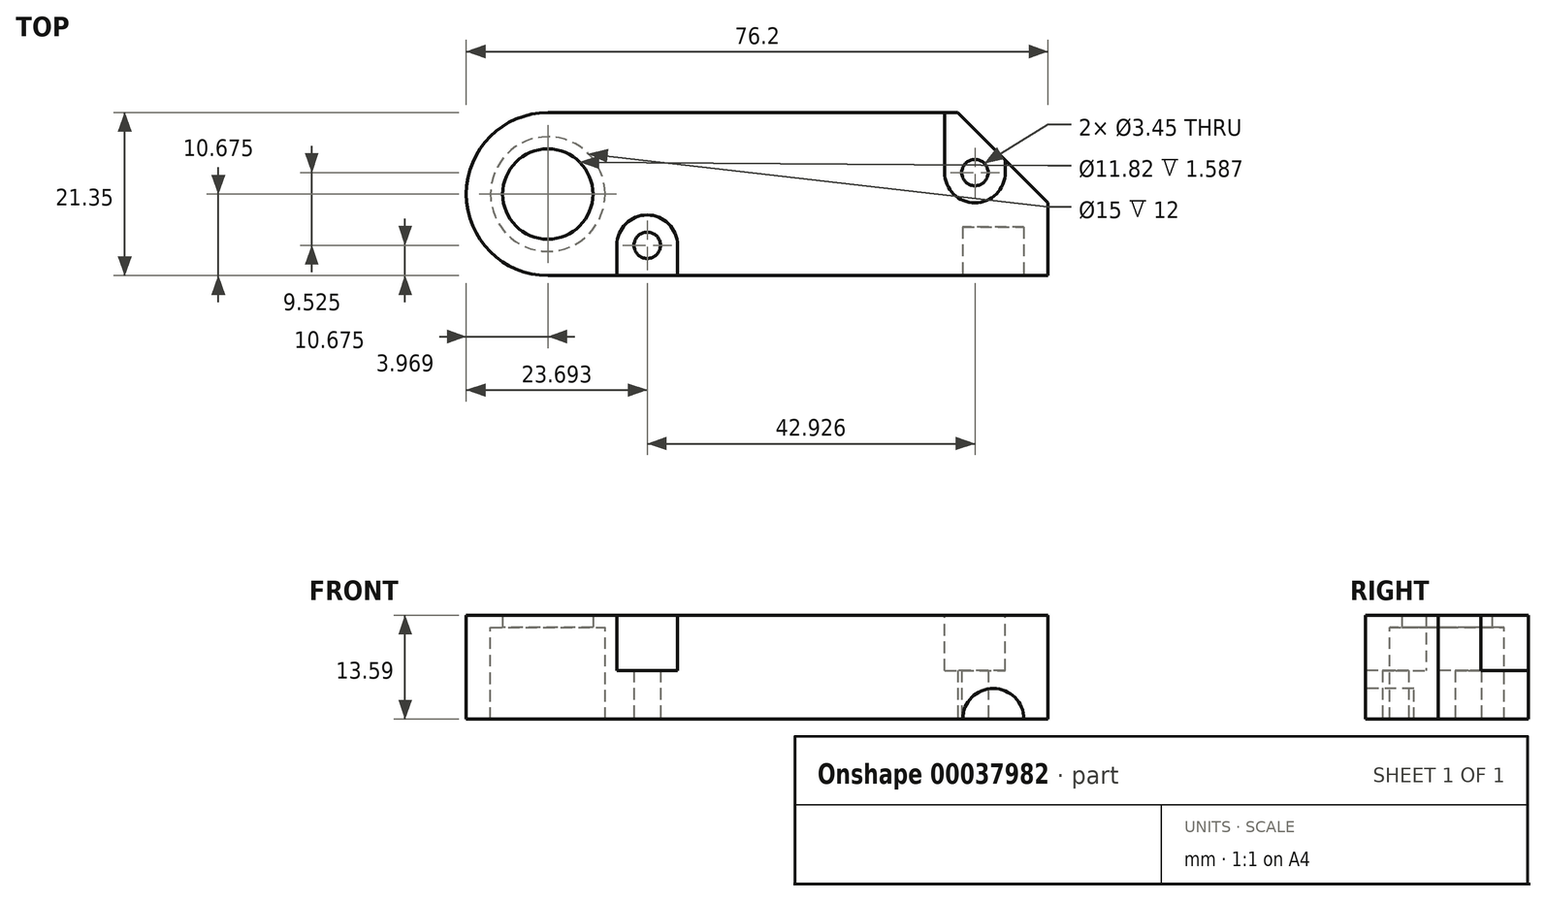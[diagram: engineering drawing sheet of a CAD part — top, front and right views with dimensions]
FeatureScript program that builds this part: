
annotation { "Feature Type Name" : "Feature", "Feature Type Description" : "" }
export const myFeature = defineFeature(function(context is Context, id is Id, definition is map)
    precondition{}
    {
        {
            var Q0;
            Q0=qCreatedBy(makeId("Top.planeOp"),FACE);
            var sketch = newSketch(context, id + "F0", { "sketchPlane" : qUnion([Q0])});
            skLineSegment(sketch, "E0.bottom", {"start": v(0, 0) * mm, "end": v(64.38, 0) * mm});
            skLineSegment(sketch, "E0.top", {"start": v(0, -21.35) * mm, "end": v(76.2, -21.35) * mm});
            skCircle(sketch, "E1", {"center": v(10.67, -10.67) * mm, "radius": 10.67 * mm, "construction": true});
            skLineSegment(sketch, "E2", {"start": v(0, 0) * mm, "end": v(0, -21.35) * mm});
            skLineSegment(sketch, "E3", {"start": v(76.2, -21.35) * mm, "end": v(76.2, -11.82) * mm});
            skLineSegment(sketch, "E4", {"start": v(76.2, -11.82) * mm, "end": v(64.38, 0) * mm});
            skCircle(sketch, "E5", {"center": v(10.67, -10.67) * mm, "radius": 5.91 * mm});
            skLineSegment(sketch, "E6", {"start": v(76.2, -11.82) * mm, "end": v(61.85, -11.82) * mm, "construction": true});
            skLineSegment(sketch, "E7", {"start": v(61.85, -11.82) * mm, "end": v(61.85, -21.35) * mm, "construction": true});
            skCircle(sketch, "E8", {"center": v(23.7, -17.38) * mm, "radius": 3.97 * mm, "construction": true});
            skCircle(sketch, "E9", {"center": v(66.62, -7.86) * mm, "radius": 3.97 * mm, "construction": true});
            skCircle(sketch, "E10", {"center": v(23.7, -17.38) * mm, "radius": 1.73 * mm});
            skCircle(sketch, "E11", {"center": v(66.62, -7.86) * mm, "radius": 1.73 * mm});
            skSolve(sketch);
        }
        {
            var Q0;
            Q0=qSketchRegion(id+"F0",true);
            extrude(context, id + "F1", {"entities" : qUnion([Q0]), "depth" : 1.59 * mm});
        }
        {
            var Q0;
            Q0=makeQuery(id+"F1.opExtrude","CAP_FACE",FACE,{"disambiguationData":[OSD([sQuery(id+"F0.wireOp",EDGE,"E0.bottom"),sQuery(id+"F0.wireOp",EDGE,"E0.top"),sQuery(id+"F0.wireOp",EDGE,"E2"),sQuery(id+"F0.wireOp",EDGE,"E3"),sQuery(id+"F0.wireOp",EDGE,"E4"),sQuery(id+"F0.wireOp",EDGE,"E5"),sQuery(id+"F0.wireOp",EDGE,"E10"),sQuery(id+"F0.wireOp",EDGE,"E11")])],"isStart":true});
            var sketch = newSketch(context, id + "F2", { "sketchPlane" : qUnion([Q0])});
            skCircle(sketch, "E12", {"center": v(10.67, 10.67) * mm, "radius": 7.5 * mm});
            skSolve(sketch);
        }
        {
            var Q0;
            Q0=makeQuery(id+"F2.imprint","IMPRINT",FACE,{"disambiguationData":[TD([[makeQuery(id+"F2.imprint","IMPRINT",EDGE,{"derivedFrom":sQuery(id+"F2.wireOp",EDGE,"E12")}),-1.0]])]});
            extrude(context, id + "F3", {"entities" : qUnion([Q0]), "operationType" : NewBodyOperationType.ADD, "depth" : 12 * mm});
        }
        {
            var Q0;
            {var subQ0=sQuery(id+"F0.wireOp",EDGE,"E0.top");Q0=makeQuery(id+"F3.boolean.opBoolean","MERGE",FACE,{"derivedFrom":[makeQuery(id+"F1.opExtrude","SWEPT_FACE",FACE,{"disambiguationData":[OSD([subQ0])]}),makeQuery(id+"F3.opExtrude","SWEPT_FACE",FACE,{"disambiguationData":[OSD([subQ0])]})]});}
            var sketch = newSketch(context, id + "F4", { "sketchPlane" : qUnion([Q0])});
            skLineSegment(sketch, "E13", {"start": v(76.2, -12) * mm, "end": v(73.03, -12) * mm});
            skLineSegment(sketch, "E14", {"start": v(73.03, -12) * mm, "end": v(65.03, -12) * mm});
            skArc(sketch, "E15", {"start": v(73.03, -12) * mm, "mid": v(69.03, -8) * mm, "end": v(65.03, -12) * mm});
            skSolve(sketch);
        }
        {
            var Q0;
            Q0=qSketchRegion(id+"F4",true);
            extrude(context, id + "F5", {"entities" : qUnion([Q0]), "operationType" : NewBodyOperationType.REMOVE, "oppositeDirection" : true, "depth" : 6.35 * mm});
        }
        {
            var Q0;
            {var subQ0=sQuery(id+"F0.wireOp",EDGE,"E2");var subQ1=sQuery(id+"F0.wireOp",EDGE,"E0.top");Q0=makeQuery(id+"F3.boolean.opBoolean","MERGE",EDGE,{"derivedFrom":[makeQuery(id+"F1.opExtrude","SWEPT_EDGE",EDGE,{"disambiguationData":[OSD([subQ1,subQ0])]}),makeQuery(id+"F3.opExtrude","SWEPT_EDGE",EDGE,{"disambiguationData":[OSD([subQ1,subQ0])]})]});}
            var Q1;
            {var subQ0=sQuery(id+"F0.wireOp",EDGE,"E2");var subQ1=sQuery(id+"F0.wireOp",EDGE,"E0.bottom");Q1=makeQuery(id+"F3.boolean.opBoolean","MERGE",EDGE,{"derivedFrom":[makeQuery(id+"F1.opExtrude","SWEPT_EDGE",EDGE,{"disambiguationData":[OSD([subQ1,subQ0])]}),makeQuery(id+"F3.opExtrude","SWEPT_EDGE",EDGE,{"disambiguationData":[OSD([subQ1,subQ0])]})]});}
            fillet(context, id + "F6", {"entities" : qUnion([Q0, Q1]), "radius" : 10.67 * mm, "tangentPropagation" : true, "allowEdgeOverflow" : false});
        }
        {
            var Q0;
            Q0=makeQuery(id+"F1.opExtrude","CAP_FACE",FACE,{"disambiguationData":[OSD([sQuery(id+"F0.wireOp",EDGE,"E0.bottom"),sQuery(id+"F0.wireOp",EDGE,"E0.top"),sQuery(id+"F0.wireOp",EDGE,"E2"),sQuery(id+"F0.wireOp",EDGE,"E3"),sQuery(id+"F0.wireOp",EDGE,"E4"),sQuery(id+"F0.wireOp",EDGE,"E5"),sQuery(id+"F0.wireOp",EDGE,"E10"),sQuery(id+"F0.wireOp",EDGE,"E11")])],"isStart":false});
            var sketch = newSketch(context, id + "F7", { "sketchPlane" : qUnion([Q0])});
            skLineSegment(sketch, "E16.rect.bottom", {"start": v(19.72, -13.41) * mm, "end": v(27.66, -13.41) * mm});
            skLineSegment(sketch, "E16.rect.top", {"start": v(19.72, -21.35) * mm, "end": v(27.66, -21.35) * mm});
            skLineSegment(sketch, "E16.rect.left", {"start": v(19.72, -13.41) * mm, "end": v(19.72, -21.35) * mm});
            skLineSegment(sketch, "E16.rect.right", {"start": v(27.66, -13.41) * mm, "end": v(27.66, -21.35) * mm});
            skPoint(sketch, "E16.rect.middle", {"position": v(23.7, -17.38) * mm});
            skLineSegment(sketch, "E17.bottom", {"start": v(62.65, 0) * mm, "end": v(64.38, 0) * mm});
            skLineSegment(sketch, "E17.top", {"start": v(62.65, -11.82) * mm, "end": v(70.59, -11.82) * mm});
            skLineSegment(sketch, "E17.left", {"start": v(62.65, -11.82) * mm, "end": v(62.65, 0) * mm});
            skLineSegment(sketch, "E17.right", {"start": v(70.59, -11.82) * mm, "end": v(70.59, -6.21) * mm});
            skLineSegment(sketch, "E18", {"start": v(66.62, -15.8) * mm, "end": v(66.62, -7.86) * mm, "construction": true});
            skPoint(sketch, "E19", {"position": v(66.62, -11.82) * mm});
            skLineSegment(sketch, "E20", {"start": v(64.38, 0) * mm, "end": v(70.59, -6.21) * mm});
            skSolve(sketch);
        }
        {
            var Q0;
            Q0=qSketchRegion(id+"F7",true);
            extrude(context, id + "F8", {"entities" : qUnion([Q0]), "operationType" : NewBodyOperationType.REMOVE, "oppositeDirection" : true, "depth" : 7.24 * mm});
        }
        {
            var Q0;
            Q0=makeQuery(id+"F8.boolean.opBoolean","COPY",EDGE,{"derivedFrom":makeQuery(id+"F8.opExtrude","SWEPT_EDGE",EDGE,{"disambiguationData":[OSD([sQuery(id+"F7.wireOp",EDGE,"E16.rect.bottom"),sQuery(id+"F7.wireOp",EDGE,"E16.rect.right")])]})});
            var Q1;
            Q1=makeQuery(id+"F8.boolean.opBoolean","COPY",EDGE,{"derivedFrom":makeQuery(id+"F8.opExtrude","SWEPT_EDGE",EDGE,{"disambiguationData":[OSD([sQuery(id+"F7.wireOp",EDGE,"E16.rect.bottom"),sQuery(id+"F7.wireOp",EDGE,"E16.rect.left")])]})});
            var Q2;
            Q2=makeQuery(id+"F8.boolean.opBoolean","COPY",EDGE,{"derivedFrom":makeQuery(id+"F8.opExtrude","SWEPT_EDGE",EDGE,{"disambiguationData":[OSD([sQuery(id+"F7.wireOp",EDGE,"E17.top"),sQuery(id+"F7.wireOp",EDGE,"E17.left")])]})});
            var Q3;
            Q3=makeQuery(id+"F8.boolean.opBoolean","COPY",EDGE,{"derivedFrom":makeQuery(id+"F8.opExtrude","SWEPT_EDGE",EDGE,{"disambiguationData":[OSD([sQuery(id+"F7.wireOp",EDGE,"E17.top"),sQuery(id+"F7.wireOp",EDGE,"E17.right")])]})});
            fillet(context, id + "F9", {"entities" : qUnion([Q0, Q1, Q2, Q3]), "radius" : 3.97 * mm, "tangentPropagation" : true, "allowEdgeOverflow" : false});
        }
    });
